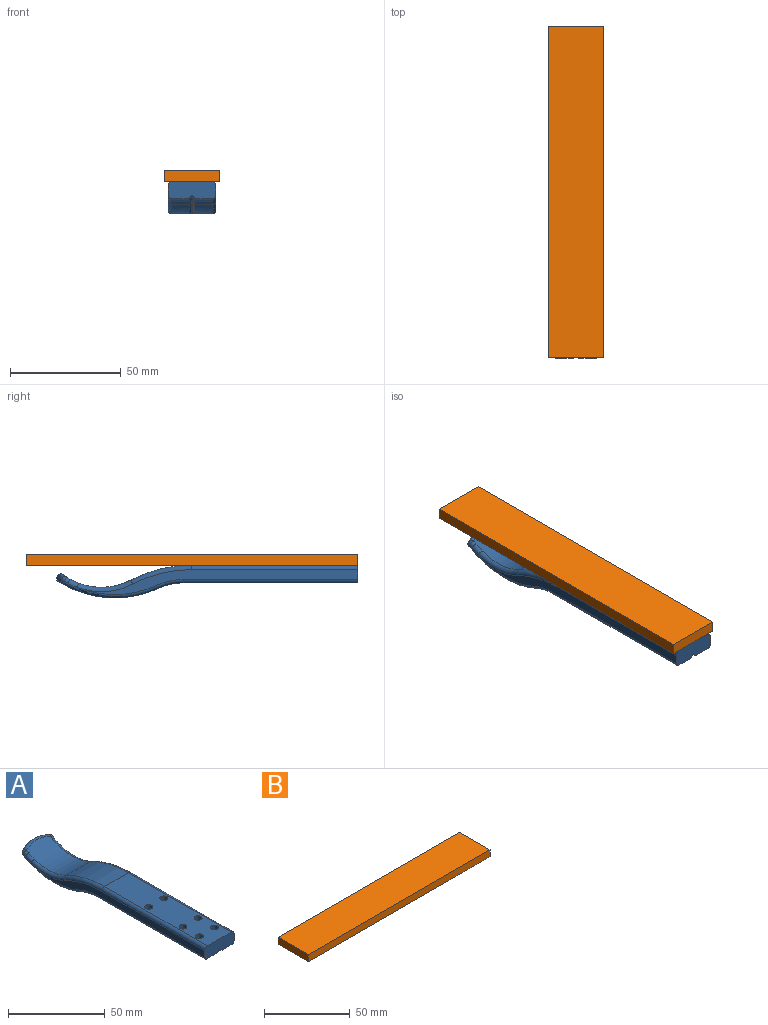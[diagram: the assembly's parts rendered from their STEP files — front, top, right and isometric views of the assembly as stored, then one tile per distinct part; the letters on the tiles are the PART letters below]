
ASSEMBLY  parts=2 mates=1
PART A: 68 faces, bbox 24.1x137.2x23.9 mm
  f0: plane 22.72x8mm, normal (0,0,-1), area 141.4mm2, adj f9,f10,f65,f67
  f1: plane 9.72x8mm, normal (0,0,-1), area 37.4mm2, adj f9,f10,f63,f67
  f2: plane 31.86x8mm, normal (0,0,-1), area 234.7mm2, adj f9,f10,f20,f65
  f3: plane 8x7.86mm, normal (0,0,-1), area 42.7mm2, adj f9,f10,f21,f63
  f4: plane 31.86x8mm, normal (0,0,-1), area 234.7mm2, adj f8,f11,f23,f61
  f5: plane 22.72x8mm, normal (0,0,-1), area 141.4mm2, adj f8,f11,f59,f61
  f6: plane 9.72x8mm, normal (0,0,-1), area 37.4mm2, adj f8,f11,f57,f59
  f7: plane 8x7.86mm, normal (0,0,-1), area 42.7mm2, adj f8,f11,f21,f57
  f8: cylinder r=1.5mm len=79mm, axis (0,1,0), area 180.8mm2, adj f4,f5,f6,f7,f21,f26,f27,f57
  f9: cylinder r=1.5mm len=79mm, axis (0,-1,0), area 182.3mm2, adj f0,f1,f2,f3,f21,f22,f28,f63
  f10: plane 79.25x1.75mm, normal (0.83,0,-0.55), area 141.9mm2, adj f0,f1,f2,f3,f21,f37,f41,f63
  f11: plane 79.06x1.56mm, normal (-0.83,0,-0.55), area 141.9mm2, adj f4,f5,f6,f7,f21,f37,f44,f57
  f12: cylinder r=46.83mm len=45.28mm, axis (1,0,0), area 817.3mm2, adj f16,f17,f20,f23,f38,f42,f43,f45
  f13: plane 1.54x0.9mm, normal (1,0,0), area 0mm2, adj f16,f18,f54
  f14: cylinder r=29mm len=30.84mm, axis (1,0,0), area 559.4mm2, adj f18,f19,f24,f29,f30,f33,f34,f50
  f15: plane 1.54x0.9mm, normal (-1,0,0), area 0mm2, adj f17,f19,f49
  f16: torus R=45.33mm, axis (1,0,0), area 104.4mm2, adj f12,f13,f26,f27,f29,f55
  f17: torus R=45.33mm, axis (1,0,0), area 104.4mm2, adj f12,f15,f22,f28,f33,f51
  f18: torus R=31mm, axis (1,0,0), area 5.5mm2, adj f13,f14,f29,f52
  f19: torus R=31mm, axis (1,0,0), area 5.5mm2, adj f14,f15,f33,f48
  f20: cylinder r=27mm len=11.32mm, axis (1,0,0), area 93.5mm2, adj f2,f12,f28,f41
  f21: plane 21.5x8mm, normal (0,-1,0), area 167.1mm2, adj f3,f7,f8,f9,f10,f11,f22,f25
  f22: plane 126.87x11.3mm, normal (-1,0,0), area 496.5mm2, adj f9,f17,f21,f28,f34,f35,f36
  f23: cylinder r=27mm len=11.32mm, axis (1,0,0), area 93.5mm2, adj f4,f12,f27,f44
  f24: cylinder r=60mm len=27.63mm, axis (1,0,0), area 502.5mm2, adj f14,f25,f31,f35
  f25: plane 75.01x17.5mm, normal (0,0,1), area 1233.5mm2, adj f21,f24,f32,f36,f56,f58,f60,f62
  f26: plane 126.87x11.3mm, normal (1,0,0), area 496.5mm2, adj f8,f16,f21,f27,f30,f31,f32
  f27: torus R=28.5mm, axis (1,0,0), area 28.1mm2, adj f8,f16,f23,f26
  f28: torus R=28.5mm, axis (1,0,0), area 28.1mm2, adj f9,f17,f20,f22
  f29: bspline ~6.95x4.69mm, area 14.1mm2, adj f14,f16,f18,f30
  f30: torus R=31mm, axis (1,0,0), area 78.2mm2, adj f14,f26,f29,f31
  f31: torus R=58mm, axis (1,0,0), area 89.1mm2, adj f24,f26,f30,f32
  f32: cylinder r=2mm len=75.01mm, axis (0,-1,0), area 235.7mm2, adj f21,f25,f26,f31
  f33: bspline ~6.95x4.69mm, area 14.1mm2, adj f14,f17,f19,f34
  f34: torus R=31mm, axis (1,0,0), area 78.2mm2, adj f14,f22,f33,f35
  f35: torus R=58mm, axis (1,0,0), area 89.1mm2, adj f22,f24,f34,f36
  f36: cylinder r=2mm len=75.01mm, axis (0,1,0), area 235.7mm2, adj f21,f22,f25,f35
  f37: plane 79x0.5mm, normal (0,0,-1), area 39.5mm2, adj f10,f11,f21,f40
  f38: cylinder r=28.5mm len=7.03mm, axis (1,0,0), area 3.7mm2, adj f12,f39,f42,f45
  f39: cylinder r=45.33mm len=12.37mm, axis (1,0,0), area 6.5mm2, adj f38,f40,f43,f46
  f40: cylinder r=28.5mm len=11.95mm, axis (1,0,0), area 6.2mm2, adj f37,f39,f41,f44
  f41: cone r=27mm half-angle=56.3deg, axis (1,0,0), area 21.6mm2, adj f10,f20,f40,f43
  f42: cone r=27mm half-angle=56.3deg, axis (1,0,0), area 8.7mm2, adj f12,f38,f43
  f43: cone r=45.33mm half-angle=56.3deg, axis (-1,0,0), area 23.7mm2, adj f12,f39,f41,f42
  f44: cone r=28.5mm half-angle=56.3deg, axis (-1,0,0), area 21.6mm2, adj f11,f23,f40,f46
  f45: cone r=28.5mm half-angle=56.3deg, axis (-1,0,0), area 8.7mm2, adj f12,f38,f46
  f46: cone r=46.83mm half-angle=56.3deg, axis (1,0,0), area 23.7mm2, adj f12,f39,f44,f45
  f47: cylinder r=20mm len=20mm, axis (0,0.57,-0.82), area 13.5mm2, adj f48,f49,f50,f52,f53,f54
  f48: bspline ~2.83x2.5mm, area 3.9mm2, adj f19,f47,f49,f50
  f49: cylinder r=1.5mm len=1.1mm, axis (0,0.57,-0.82), area 0.1mm2, adj f15,f47,f48,f51
  f50: bspline ~22.57x4.67mm, area 45.4mm2, adj f14,f47,f48,f52
  f51: sphere r=1.5mm, area 2.7mm2, adj f17,f49,f53
  f52: bspline ~3.08x2.5mm, area 3.9mm2, adj f18,f47,f50,f54
  f53: bspline ~23.83x4.48mm, area 49.6mm2, adj f12,f47,f51,f55
  f54: cylinder r=1.5mm len=1.1mm, axis (0,0.57,-0.82), area 0.1mm2, adj f13,f47,f52,f55
  f55: sphere r=1.5mm, area 2.7mm2, adj f16,f53,f54
  f56: cylinder r=2.05mm len=5.65mm, axis (0,0,-1), area 72.8mm2, adj f25,f57
  f57: cone r=2.05mm half-angle=45deg, axis (0,0,-1), area 67.2mm2, adj f6,f7,f8,f11,f56
  f58: cylinder r=2.05mm len=5.65mm, axis (0,0,-1), area 72.8mm2, adj f25,f59
  f59: cone r=2.05mm half-angle=45deg, axis (0,0,-1), area 67.2mm2, adj f5,f6,f8,f11,f58
  f60: cylinder r=2.05mm len=5.65mm, axis (0,0,-1), area 72.8mm2, adj f25,f61
  f61: cone r=2.05mm half-angle=45deg, axis (0,0,-1), area 67.2mm2, adj f4,f5,f8,f11,f60
  f62: cylinder r=2.05mm len=5.65mm, axis (0,0,-1), area 72.8mm2, adj f25,f63
  f63: cone r=2.05mm half-angle=45deg, axis (0,0,-1), area 67mm2, adj f1,f3,f9,f10,f62
  f64: cylinder r=2.05mm len=5.65mm, axis (0,0,-1), area 72.8mm2, adj f25,f65
  f65: cone r=2.05mm half-angle=45deg, axis (0,0,-1), area 67mm2, adj f0,f2,f9,f10,f64
  f66: cylinder r=2.05mm len=5.65mm, axis (0,0,-1), area 72.8mm2, adj f25,f67
  f67: cone r=2.05mm half-angle=45deg, axis (0,0,-1), area 67mm2, adj f0,f1,f9,f10,f66
PART B: 6 faces, bbox 150x25x5 mm
  f0: plane 25x5mm, normal (-1,0,0), area 125mm2, adj f1,f3,f4,f5
  f1: plane 150x25mm, normal (0,0,-1), area 3750mm2, adj f0,f2,f4,f5
  f2: plane 25x5mm, normal (1,0,0), area 125mm2, adj f1,f3,f4,f5
  f3: plane 150x25mm, normal (0,0,1), area 3750mm2, adj f0,f2,f4,f5
  f4: plane 150x5mm, normal (0,-1,0), area 750mm2, adj f0,f1,f2,f3
  f5: plane 150x5mm, normal (0,1,0), area 750mm2, adj f0,f1,f2,f3
PLACE A t=(-4.6,-57.8,22.36)mm fixed
PLACE B rot(axis=(0,0,1),90deg) t=(-17.1,-67.8,22.36)mm
MATE fastened B.f1 <-> A.f25  axis (0,0,-1) through (-4.6,-67.8,22.36)mm
